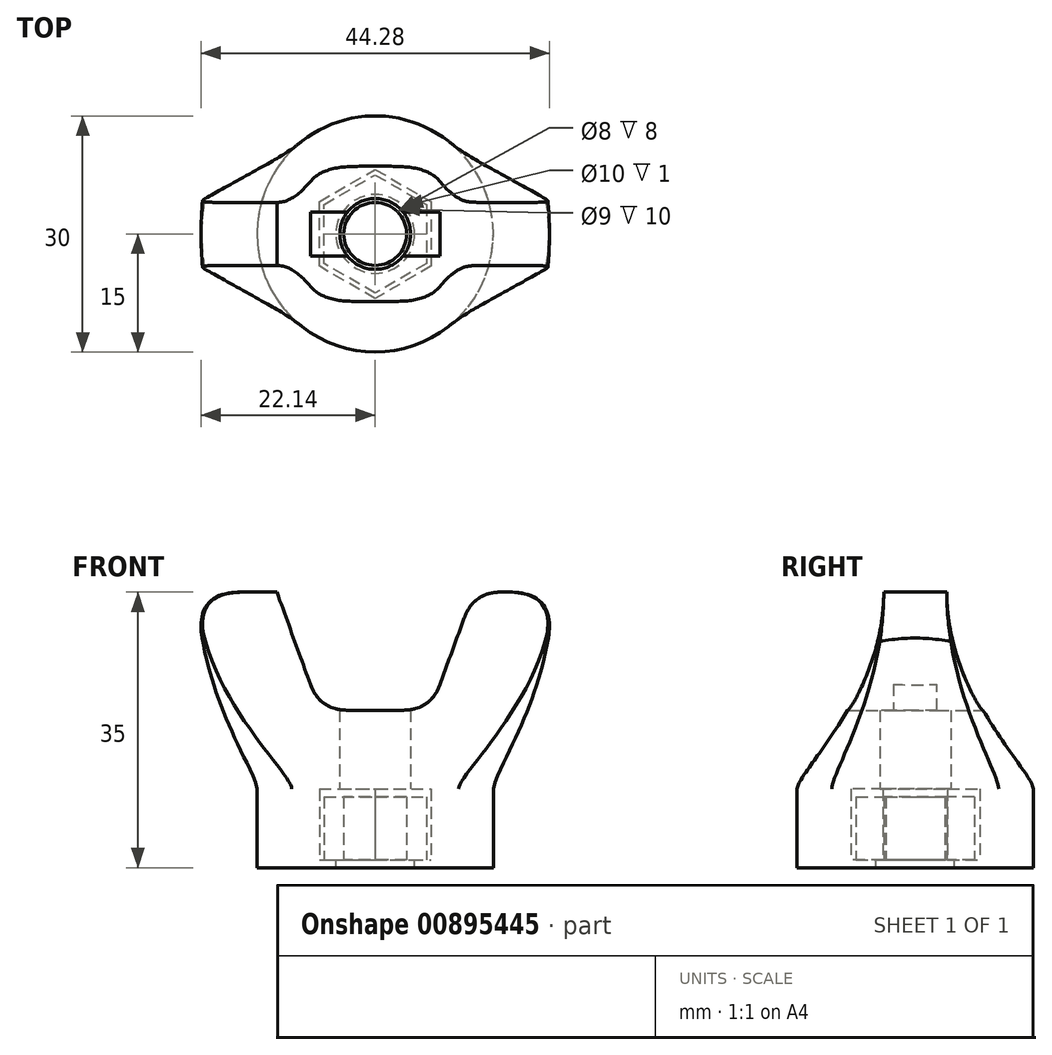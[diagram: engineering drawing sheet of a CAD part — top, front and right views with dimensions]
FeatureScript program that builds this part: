
annotation { "Feature Type Name" : "Feature", "Feature Type Description" : "" }
export const myFeature = defineFeature(function(context is Context, id is Id, definition is map)
    precondition{}
    {
        {
            var Q0;
            Q0=qCreatedBy(makeId("Top.planeOp"),FACE);
            var sketch = newSketch(context, id + "F0", { "sketchPlane" : qUnion([Q0])});
            skCircle(sketch, "E0.cCircle", {"center": v(0, 0) * mm, "radius": 6.5 * mm, "construction": true});
            skLineSegment(sketch, "E0.0", {"start": v(0, 7.5) * mm, "end": v(6.5, 3.75) * mm});
            skLineSegment(sketch, "E0.1", {"start": v(6.5, 3.75) * mm, "end": v(6.5, -3.75) * mm});
            skLineSegment(sketch, "E0.2", {"start": v(6.5, -3.75) * mm, "end": v(0, -7.5) * mm});
            skLineSegment(sketch, "E0.3", {"start": v(0, -7.5) * mm, "end": v(-6.5, -3.75) * mm});
            skLineSegment(sketch, "E0.4", {"start": v(-6.5, -3.75) * mm, "end": v(-6.5, 3.75) * mm});
            skLineSegment(sketch, "E0.5", {"start": v(-6.5, 3.75) * mm, "end": v(0, 7.5) * mm});
            skPoint(sketch, "E0.0.midPoint", {"position": v(3.25, 5.63) * mm});
            skCircle(sketch, "E1", {"center": v(0, 0) * mm, "radius": 4 * mm});
            skSolve(sketch);
        }
        {
            var Q0;
            Q0=makeQuery(id+"F0.imprint","IMPRINT",FACE,{"disambiguationData":[TD([[makeQuery(id+"F0.imprint","IMPRINT",EDGE,{"derivedFrom":sQuery(id+"F0.wireOp",EDGE,"E0.0")}),-1.0]])]});
            extrude(context, id + "F1", {"entities" : qUnion([Q0]), "depth" : 8 * mm, "offsetDistance" : 25 * mm});
        }
        {
            var Q0;
            Q0=qCreatedBy(makeId("Top.planeOp"),FACE);
            var sketch = newSketch(context, id + "F2", { "sketchPlane" : qUnion([Q0])});
            skCircle(sketch, "E2", {"center": v(0, 0) * mm, "radius": 15 * mm});
            skLineSegment(sketch, "E3.0", {"start": v(-7.1, 4.1) * mm, "end": v(0, 8.2) * mm});
            skLineSegment(sketch, "E3.1", {"start": v(7.1, 4.1) * mm, "end": v(7.1, -4.1) * mm});
            skLineSegment(sketch, "E3.2", {"start": v(7.1, -4.1) * mm, "end": v(0, -8.2) * mm});
            skLineSegment(sketch, "E3.3", {"start": v(0, 8.2) * mm, "end": v(7.1, 4.1) * mm});
            skLineSegment(sketch, "E3.4", {"start": v(0, -8.2) * mm, "end": v(-7.1, -4.1) * mm});
            skLineSegment(sketch, "E3.5", {"start": v(-7.1, -4.1) * mm, "end": v(-7.1, 4.1) * mm});
            skSolve(sketch);
        }
        {
            var Q0;
            Q0=makeQuery(id+"F2.imprint","IMPRINT",FACE,{"disambiguationData":[TD([[makeQuery(id+"F2.imprint","IMPRINT",EDGE,{"derivedFrom":sQuery(id+"F2.wireOp",EDGE,"E2")}),1.0]])]});
            extrude(context, id + "F3", {"entities" : qUnion([Q0]), "depth" : 9 * mm, "offsetDistance" : 25 * mm});
        }
        {
            var Q0;
            Q0=makeQuery(id+"F3.opExtrude","CAP_FACE",FACE,{"disambiguationData":[OSD([sQuery(id+"F2.wireOp",EDGE,"E2"),sQuery(id+"F2.wireOp",EDGE,"E3.0"),sQuery(id+"F2.wireOp",EDGE,"E3.1"),sQuery(id+"F2.wireOp",EDGE,"E3.2"),sQuery(id+"F2.wireOp",EDGE,"E3.3"),sQuery(id+"F2.wireOp",EDGE,"E3.4"),sQuery(id+"F2.wireOp",EDGE,"E3.5")])],"isStart":true});
            var sketch = newSketch(context, id + "F4", { "sketchPlane" : qUnion([Q0])});
            skCircle(sketch, "E4", {"center": v(0, 0) * mm, "radius": 5 * mm});
            skCircle(sketch, "E5.0", {"center": v(0, 0) * mm, "radius": 15 * mm});
            skSolve(sketch);
        }
        {
            var Q0;
            Q0=makeQuery(id+"F4.imprint","IMPRINT",FACE,{"disambiguationData":[TD([[makeQuery(id+"F4.imprint","IMPRINT",EDGE,{"derivedFrom":sQuery(id+"F4.wireOp",EDGE,"E5.0")}),-1.0]])]});
            var Q1;
            Q1=makeQuery(id+"F4.imprint","IMPRINT",FACE,{"disambiguationData":[TD([[makeQuery(id+"F4.imprint","IMPRINT",EDGE,{"derivedFrom":sQuery(id+"F4.wireOp",EDGE,"E4")}),-1.0]])]});
            extrude(context, id + "F5", {"entities" : qUnion([Q0, Q1]), "operationType" : NewBodyOperationType.ADD, "depth" : 1 * mm, "offsetDistance" : 25 * mm});
        }
        {
            var Q0;
            Q0=makeQuery(id+"F3.opExtrude","CAP_FACE",FACE,{"disambiguationData":[OSD([sQuery(id+"F2.wireOp",EDGE,"E2"),sQuery(id+"F2.wireOp",EDGE,"E3.0"),sQuery(id+"F2.wireOp",EDGE,"E3.1"),sQuery(id+"F2.wireOp",EDGE,"E3.2"),sQuery(id+"F2.wireOp",EDGE,"E3.3"),sQuery(id+"F2.wireOp",EDGE,"E3.4"),sQuery(id+"F2.wireOp",EDGE,"E3.5")])],"isStart":false});
            cPlane(context, id + "F6", {"entities" : qUnion([Q0]), "cplaneType" : CPlaneType.OFFSET, "offset" : 25 * mm, "width" : 150 * mm, "height" : 150 * mm});
        }
        {
            var Q0;
            Q0=qCreatedBy(id+"F6.planeOp",FACE);
            var sketch = newSketch(context, id + "F7", { "sketchPlane" : qUnion([Q0])});
            skLineSegment(sketch, "E6.bottom", {"start": v(22.5, 4) * mm, "end": v(-22.5, 4) * mm});
            skLineSegment(sketch, "E6.top", {"start": v(22.5, -4) * mm, "end": v(-22.5, -4) * mm});
            skLineSegment(sketch, "E6.left", {"start": v(22.5, 4) * mm, "end": v(22.5, -4) * mm});
            skLineSegment(sketch, "E6.right", {"start": v(-22.5, 4) * mm, "end": v(-22.5, -4) * mm});
            skPoint(sketch, "E6.middle", {"position": v(0, 0) * mm});
            skSolve(sketch);
        }
        {
            var Q0;
            Q0=makeQuery(id+"F3.opExtrude","CAP_FACE",FACE,{"disambiguationData":[OSD([sQuery(id+"F2.wireOp",EDGE,"E2"),sQuery(id+"F2.wireOp",EDGE,"E3.0"),sQuery(id+"F2.wireOp",EDGE,"E3.1"),sQuery(id+"F2.wireOp",EDGE,"E3.2"),sQuery(id+"F2.wireOp",EDGE,"E3.3"),sQuery(id+"F2.wireOp",EDGE,"E3.4"),sQuery(id+"F2.wireOp",EDGE,"E3.5")])],"isStart":false});
            var sketch = newSketch(context, id + "F8", { "sketchPlane" : qUnion([Q0])});
            skCircle(sketch, "E7.0", {"center": v(0, 0) * mm, "radius": 15 * mm});
            skLineSegment(sketch, "E8", {"start": v(-10.6, 10.6) * mm, "end": v(10.6, -10.6) * mm, "construction": true});
            skLineSegment(sketch, "E9", {"start": v(10.6, 10.6) * mm, "end": v(-10.6, -10.6) * mm, "construction": true});
            skSolve(sketch);
        }
        {
            var Q1;
            Q1 = qSketchRegion(id + "F8", true);
            var Q2;
            Q2=makeQuery(id+"F7.imprint","IMPRINT",FACE,{"disambiguationData":[TD([[makeQuery(id+"F7.imprint","IMPRINT",EDGE,{"derivedFrom":sQuery(id+"F7.wireOp",EDGE,"E6.bottom")}),1.0]])]});
            var Q3;
            Q3=sQuery(id+"F8.wireOp",VERTEX,"E8.start");
            var Q4;
            Q4=sQuery(id+"F7.wireOp",VERTEX,"E6.bottom.end");
            loft(context, id + "F9", {"operationType" : NewBodyOperationType.ADD, "startCondition" : LoftEndDerivativeType.NORMAL_TO_PROFILE, "startMagnitude" : .25, "endCondition" : LoftEndDerivativeType.NORMAL_TO_PROFILE, "endMagnitude" : 1.5, "sheetProfilesArray" : [{ "sheetProfileEntities" : qUnion([Q1]) }, { "sheetProfileEntities" : qUnion([Q2]) }], "matchConnections" : true, "connections" : [{ "connectionEntities" : qUnion([Q3, Q4]), "connectionEdgeQueries" : qUnion([]), "connectionEdgeParameters" : [] }]});
        }
        {
            var Q0;
            Q0=qCreatedBy(makeId("Front.planeOp"),FACE);
            var sketch = newSketch(context, id + "F10", { "sketchPlane" : qUnion([Q0])});
            skLineSegment(sketch, "E10", {"start": v(-12.5, 34) * mm, "end": v(-7.04, 19) * mm});
            skLineSegment(sketch, "E11", {"start": v(12.5, 34) * mm, "end": v(7.04, 19) * mm});
            skLineSegment(sketch, "E12", {"start": v(-7.04, 19) * mm, "end": v(7.04, 19) * mm});
            skLineSegment(sketch, "E13", {"start": v(-12.5, 34) * mm, "end": v(12.5, 34) * mm});
            skSolve(sketch);
        }
        {
            var Q0;
            Q0 = qSketchRegion(id + "F10", true);
            extrude(context, id + "F11", {"entities" : qUnion([Q0]), "operationType" : NewBodyOperationType.REMOVE, "endBound" : BoundingType.THROUGH_ALL, "oppositeDirection" : true, "depth" : 25 * mm, "offsetDistance" : 25 * mm, "hasSecondDirection" : true, "secondDirectionBound" : SecondDirectionBoundingType.THROUGH_ALL, "secondDirectionOppositeDirection" : false, "secondDirectionDepth" : 25 * mm});
        }
        {
            var Q0;
            Q0=makeQuery(id+"F9.opLoft","CAP_FACE",FACE,{"disambiguationData":[OSD([makeQuery(id+"F8.imprint","IMPRINT",FACE,{"disambiguationData":[TD([[makeQuery(id+"F8.imprint","IMPRINT",EDGE,{"derivedFrom":makeQuery(id+"F3.opExtrude","CAP_EDGE",EDGE,{"disambiguationData":[OSD([sQuery(id+"F2.wireOp",EDGE,"E3.0")])],"isStart":false})}),-1.0]])]})])],"isStart":true});
            var sketch = newSketch(context, id + "F12", { "sketchPlane" : qUnion([Q0])});
            skCircle(sketch, "E14", {"center": v(0, 0) * mm, "radius": 4.5 * mm});
            skSolve(sketch);
        }
        {
            var Q0;
            Q0=makeQuery(id+"F12.imprint","IMPRINT",FACE,{"disambiguationData":[TD([[makeQuery(id+"F12.imprint","IMPRINT",EDGE,{"derivedFrom":sQuery(id+"F12.wireOp",EDGE,"E14")}),1.0]])]});
            extrude(context, id + "F13", {"entities" : qUnion([Q0]), "operationType" : NewBodyOperationType.REMOVE, "endBound" : BoundingType.THROUGH_ALL, "oppositeDirection" : true, "depth" : 25 * mm, "offsetDistance" : 25 * mm});
        }
        {
            var Q0;
            Q0=makeQuery(id+"F9.opLoft","MID_CAP_EDGE",EDGE,{"disambiguationData":[OSD([sQuery(id+"F7.wireOp",EDGE,"E6.bottom"),sQuery(id+"F7.wireOp",EDGE,"E6.top"),sQuery(id+"F7.wireOp",EDGE,"E6.right")])],"capPos":1.0});
            var Q1;
            Q1=makeQuery(id+"F11.boolean.opBoolean","COPY",EDGE,{"derivedFrom":makeQuery(id+"F11.opExtrude","SWEPT_EDGE",EDGE,{"disambiguationData":[OSD([sQuery(id+"F10.wireOp",EDGE,"E10"),sQuery(id+"F10.wireOp",EDGE,"E13")])]})});
            var Q2;
            Q2=makeQuery(id+"F11.boolean.opBoolean","COPY",EDGE,{"derivedFrom":makeQuery(id+"F11.opExtrude","SWEPT_EDGE",EDGE,{"disambiguationData":[OSD([sQuery(id+"F10.wireOp",EDGE,"E11"),sQuery(id+"F10.wireOp",EDGE,"E13")])]})});
            var Q3;
            Q3=makeQuery(id+"F9.opLoft","MID_CAP_EDGE",EDGE,{"disambiguationData":[OSD([sQuery(id+"F7.wireOp",EDGE,"E6.bottom"),sQuery(id+"F7.wireOp",EDGE,"E6.top"),sQuery(id+"F7.wireOp",EDGE,"E6.left")])],"capPos":1.0});
            var Q4;
            Q4=makeQuery(id+"F11.boolean.opBoolean","COPY",EDGE,{"derivedFrom":makeQuery(id+"F11.opExtrude","SWEPT_EDGE",EDGE,{"disambiguationData":[OSD([sQuery(id+"F10.wireOp",EDGE,"E10"),sQuery(id+"F10.wireOp",EDGE,"E12")])]})});
            var Q5;
            Q5=makeQuery(id+"F11.boolean.opBoolean","COPY",EDGE,{"derivedFrom":makeQuery(id+"F11.opExtrude","SWEPT_EDGE",EDGE,{"disambiguationData":[OSD([sQuery(id+"F10.wireOp",EDGE,"E11"),sQuery(id+"F10.wireOp",EDGE,"E12")])]})});
            fillet(context, id + "F14", {"entities" : qUnion([Q0, Q1, Q2, Q3, Q4, Q5]), "radius" : 5 * mm, "tangentPropagation" : true, "rho" : 0.5, "crossSection" : FilletCrossSection.CONIC, "allowEdgeOverflow" : false});
        }
    });
